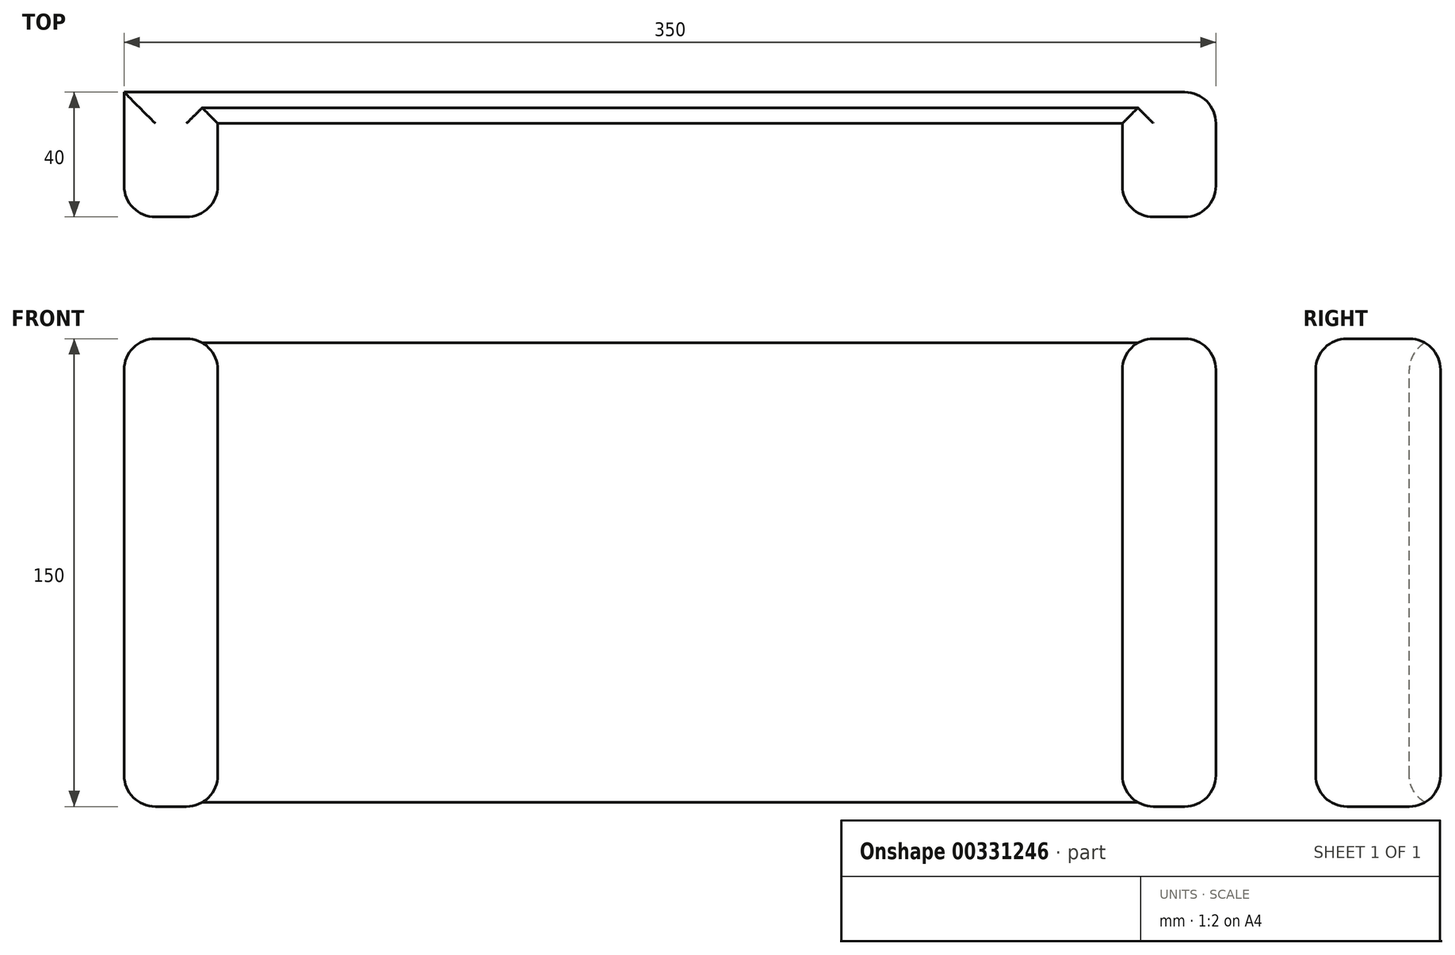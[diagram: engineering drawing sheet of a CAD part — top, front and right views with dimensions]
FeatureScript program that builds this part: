
annotation { "Feature Type Name" : "Feature", "Feature Type Description" : "" }
export const myFeature = defineFeature(function(context is Context, id is Id, definition is map)
    precondition{}
    {
        {
            var Q0;
            Q0=qCreatedBy(makeId("Front.planeOp"),FACE);
            var sketch = newSketch(context, id + "F0", { "sketchPlane" : qUnion([Q0])});
            skLineSegment(sketch, "E0.bottom", {"start": v(175, -75) * mm, "end": v(-175, -75) * mm});
            skLineSegment(sketch, "E0.top", {"start": v(175, 75) * mm, "end": v(-175, 75) * mm});
            skLineSegment(sketch, "E0.left", {"start": v(175, -75) * mm, "end": v(175, 75) * mm});
            skLineSegment(sketch, "E0.right", {"start": v(-175, -75) * mm, "end": v(-175, 75) * mm});
            skPoint(sketch, "E0.middle", {"position": v(0, 0) * mm});
            skSolve(sketch);
        }
        {
            var Q0;
            Q0 = qSketchRegion(id + "F0", true);
            extrude(context, id + "F1", {"entities" : qUnion([Q0]), "depth" : 10 * mm});
        }
        {
            var Q0;
            Q0=makeQuery(id+"F1.opExtrude","CAP_FACE",FACE,{"disambiguationData":[OSD([sQuery(id+"F0.wireOp",EDGE,"E0.bottom"),sQuery(id+"F0.wireOp",EDGE,"E0.top"),sQuery(id+"F0.wireOp",EDGE,"E0.left"),sQuery(id+"F0.wireOp",EDGE,"E0.right")])],"isStart":true});
            var sketch = newSketch(context, id + "F2", { "sketchPlane" : qUnion([Q0])});
            skLineSegment(sketch, "E1.bottom", {"start": v(-175, 75) * mm, "end": v(-145, 75) * mm});
            skLineSegment(sketch, "E1.top", {"start": v(-175, -75) * mm, "end": v(-145, -75) * mm});
            skLineSegment(sketch, "E1.left", {"start": v(-175, 75) * mm, "end": v(-175, -75) * mm});
            skLineSegment(sketch, "E1.right", {"start": v(-145, 75) * mm, "end": v(-145, -75) * mm});
            skLineSegment(sketch, "E2.bottom", {"start": v(175, 75) * mm, "end": v(145, 75) * mm});
            skLineSegment(sketch, "E2.top", {"start": v(175, -75) * mm, "end": v(145, -75) * mm});
            skLineSegment(sketch, "E2.left", {"start": v(175, 75) * mm, "end": v(175, -75) * mm});
            skLineSegment(sketch, "E2.right", {"start": v(145, 75) * mm, "end": v(145, -75) * mm});
            skSolve(sketch);
        }
        {
            var Q0;
            Q0 = qSketchRegion(id + "F2", true);
            extrude(context, id + "F3", {"entities" : qUnion([Q0]), "operationType" : NewBodyOperationType.ADD, "oppositeDirection" : true, "depth" : 40 * mm});
        }
        {
            var Q0;
            Q0=makeQuery(id+"F3.opExtrude","CAP_EDGE",EDGE,{"disambiguationData":[OSD([sQuery(id+"F2.wireOp",EDGE,"E1.bottom")])],"isStart":false});
            var Q1;
            Q1=makeQuery(id+"F3.opExtrude","SWEPT_EDGE",EDGE,{"disambiguationData":[OSD([sQuery(id+"F0.wireOp",EDGE,"E0.top"),sQuery(id+"F2.wireOp",EDGE,"E1.bottom"),sQuery(id+"F2.wireOp",EDGE,"E1.right")])]});
            var Q2;
            Q2=makeQuery(id+"F3.boolean.opBoolean","MERGE",EDGE,{"derivedFrom":[makeQuery(id+"F1.opExtrude","SWEPT_EDGE",EDGE,{"disambiguationData":[OSD([sQuery(id+"F0.wireOp",EDGE,"E0.bottom"),sQuery(id+"F0.wireOp",EDGE,"E0.left")])]}),makeQuery(id+"F3.opExtrude","SWEPT_EDGE",EDGE,{"disambiguationData":[OSD([sQuery(id+"F2.wireOp",EDGE,"E1.top"),sQuery(id+"F2.wireOp",EDGE,"E1.left")])]})]});
            var Q3;
            Q3=makeQuery(id+"F3.opExtrude","CAP_EDGE",EDGE,{"disambiguationData":[OSD([sQuery(id+"F2.wireOp",EDGE,"E1.left")])],"isStart":false});
            var Q4;
            Q4=makeQuery(id+"F3.opExtrude","CAP_EDGE",EDGE,{"disambiguationData":[OSD([sQuery(id+"F2.wireOp",EDGE,"E1.top")])],"isStart":false});
            var Q5;
            Q5=makeQuery(id+"F3.opExtrude","SWEPT_EDGE",EDGE,{"disambiguationData":[OSD([sQuery(id+"F0.wireOp",EDGE,"E0.bottom"),sQuery(id+"F2.wireOp",EDGE,"E1.top"),sQuery(id+"F2.wireOp",EDGE,"E1.right")])]});
            var Q6;
            Q6=makeQuery(id+"F3.boolean.opBoolean","MERGE",FACE,{"derivedFrom":[makeQuery(id+"F1.opExtrude","SWEPT_FACE",FACE,{"disambiguationData":[OSD([sQuery(id+"F0.wireOp",EDGE,"E0.left")])]}),makeQuery(id+"F3.opExtrude","SWEPT_FACE",FACE,{"disambiguationData":[OSD([sQuery(id+"F2.wireOp",EDGE,"E1.left")])]})]});
            var Q7;
            Q7=makeQuery(id+"F3.opExtrude","SWEPT_EDGE",EDGE,{"disambiguationData":[OSD([sQuery(id+"F0.wireOp",EDGE,"E0.bottom"),sQuery(id+"F2.wireOp",EDGE,"E2.top"),sQuery(id+"F2.wireOp",EDGE,"E2.right")])]});
            var Q8;
            Q8=makeQuery(id+"F3.opExtrude","CAP_EDGE",EDGE,{"disambiguationData":[OSD([sQuery(id+"F2.wireOp",EDGE,"E2.left")])],"isStart":false});
            var Q9;
            Q9=makeQuery(id+"F3.boolean.opBoolean","MERGE",EDGE,{"derivedFrom":[makeQuery(id+"F1.opExtrude","SWEPT_EDGE",EDGE,{"disambiguationData":[OSD([sQuery(id+"F0.wireOp",EDGE,"E0.bottom"),sQuery(id+"F0.wireOp",EDGE,"E0.right")])]}),makeQuery(id+"F3.opExtrude","SWEPT_EDGE",EDGE,{"disambiguationData":[OSD([sQuery(id+"F2.wireOp",EDGE,"E2.top"),sQuery(id+"F2.wireOp",EDGE,"E2.left")])]})]});
            var Q10;
            Q10=makeQuery(id+"F3.boolean.opBoolean","MERGE",FACE,{"derivedFrom":[makeQuery(id+"F1.opExtrude","SWEPT_FACE",FACE,{"disambiguationData":[OSD([sQuery(id+"F0.wireOp",EDGE,"E0.top")])]}),makeQuery(id+"F3.opExtrude","SWEPT_FACE",FACE,{"disambiguationData":[OSD([sQuery(id+"F2.wireOp",EDGE,"E1.bottom")])]}),makeQuery(id+"F3.opExtrude","SWEPT_FACE",FACE,{"disambiguationData":[OSD([sQuery(id+"F2.wireOp",EDGE,"E2.bottom")])]})]});
            var Q11;
            Q11=makeQuery(id+"F3.boolean.opBoolean","MERGE",FACE,{"derivedFrom":[makeQuery(id+"F1.opExtrude","SWEPT_FACE",FACE,{"disambiguationData":[OSD([sQuery(id+"F0.wireOp",EDGE,"E0.bottom")])]}),makeQuery(id+"F3.opExtrude","SWEPT_FACE",FACE,{"disambiguationData":[OSD([sQuery(id+"F2.wireOp",EDGE,"E1.top")])]}),makeQuery(id+"F3.opExtrude","SWEPT_FACE",FACE,{"disambiguationData":[OSD([sQuery(id+"F2.wireOp",EDGE,"E2.top")])]})]});
            var Q12;
            Q12=makeQuery(id+"F3.opExtrude","CAP_EDGE",EDGE,{"disambiguationData":[OSD([sQuery(id+"F2.wireOp",EDGE,"E1.right")])],"isStart":false});
            var Q13;
            Q13=makeQuery(id+"F3.opExtrude","CAP_EDGE",EDGE,{"disambiguationData":[OSD([sQuery(id+"F2.wireOp",EDGE,"E2.right")])],"isStart":false});
            fillet(context, id + "F4", {"entities" : qUnion([Q0, Q1, Q2, Q3, Q4, Q5, Q6, Q7, Q8, Q9, Q10, Q11, Q12, Q13]), "radius" : 10 * mm, "tangentPropagation" : true, "allowEdgeOverflow" : false});
        }
    });
